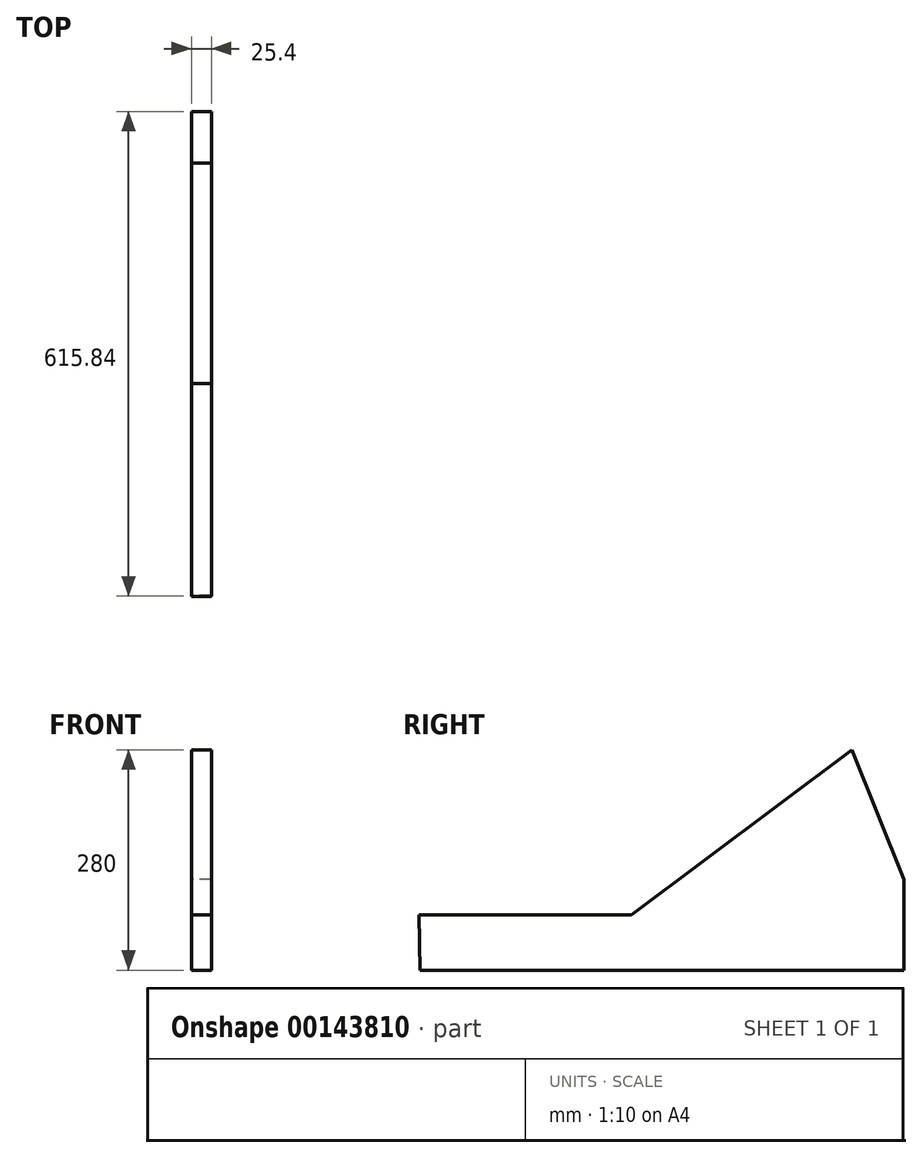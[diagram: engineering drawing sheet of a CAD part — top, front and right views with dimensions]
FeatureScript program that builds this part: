
annotation { "Feature Type Name" : "Feature", "Feature Type Description" : "" }
export const myFeature = defineFeature(function(context is Context, id is Id, definition is map)
    precondition{}
    {
        {
            var Q0;
            Q0=qCreatedBy(makeId("Right.planeOp"),FACE);
            var sketch = newSketch(context, id + "F0", { "sketchPlane" : qUnion([Q0])});
            skLineSegment(sketch, "E0", {"start": v(-7825.9, 353.89) * mm, "end": v(-7210.9, 353.89) * mm});
            skLineSegment(sketch, "E1", {"start": v(-7210.9, 353.89) * mm, "end": v(-7210.9, 468.89) * mm});
            skLineSegment(sketch, "E2", {"start": v(-7276.75, 633.89) * mm, "end": v(-7556.74, 423.88) * mm});
            skLineSegment(sketch, "E3", {"start": v(-7556.74, 423.88) * mm, "end": v(-7826.74, 423.88) * mm});
            skLineSegment(sketch, "E4", {"start": v(-7826.74, 423.88) * mm, "end": v(-7825.9, 353.89) * mm});
            skLineSegment(sketch, "E5", {"start": v(-7276.75, 633.89) * mm, "end": v(-7210.9, 468.89) * mm});
            skSolve(sketch);
        }
        {
            var Q0;
            Q0 = qSketchRegion(id + "F0", true);
            extrude(context, id + "F1", {"entities" : qUnion([Q0]), "depth" : 25.4 * mm});
        }
    });
